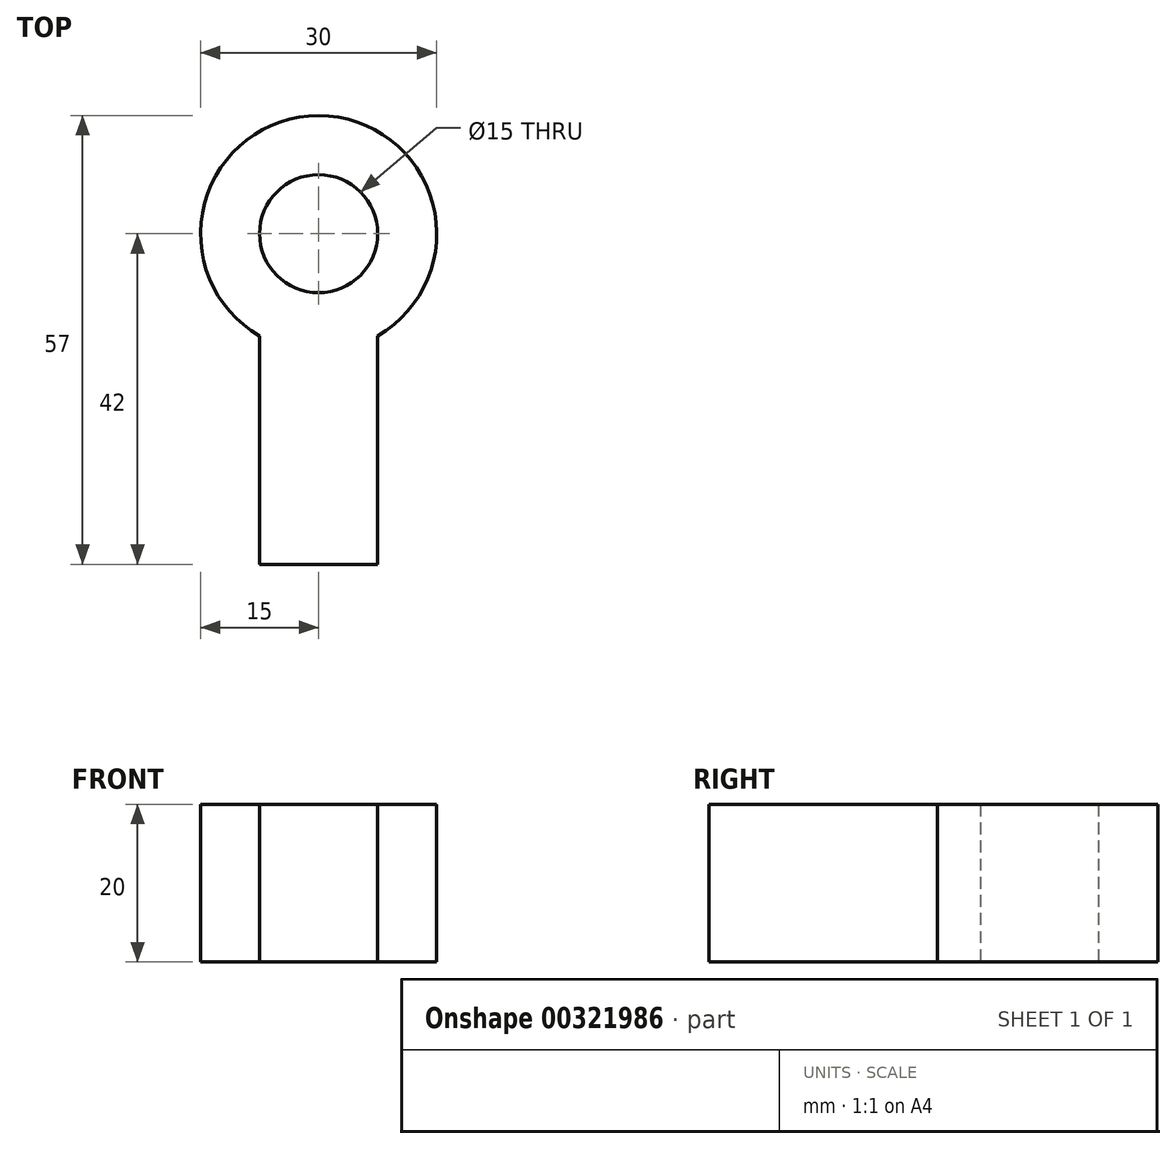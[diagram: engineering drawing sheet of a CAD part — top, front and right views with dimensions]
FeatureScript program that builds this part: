
annotation { "Feature Type Name" : "Feature", "Feature Type Description" : "" }
export const myFeature = defineFeature(function(context is Context, id is Id, definition is map)
    precondition{}
    {
        {
            var Q0;
            Q0=qCreatedBy(makeId("Top.planeOp"),FACE);
            var sketch = newSketch(context, id + "F0", { "sketchPlane" : qUnion([Q0])});
            skCircle(sketch, "E0", {"center": v(0, 0) * mm, "radius": 15 * mm});
            skCircle(sketch, "E1.0", {"center": v(0, 0) * mm, "radius": 7.5 * mm});
            skSolve(sketch);
        }
        {
            var Q0;
            Q0=makeQuery(id+"F0.imprint","IMPRINT",FACE,{"disambiguationData":[TD([[makeQuery(id+"F0.imprint","IMPRINT",EDGE,{"derivedFrom":sQuery(id+"F0.wireOp",EDGE,"E0")}),1.0]])]});
            extrude(context, id + "F1", {"entities" : qUnion([Q0]), "depth" : 20 * mm});
        }
        {
            var Q0;
            Q0=qCreatedBy(makeId("Front.planeOp"),FACE);
            cPlane(context, id + "F2", {"entities" : qUnion([Q0]), "cplaneType" : CPlaneType.OFFSET, "offset" : 12 * mm, "width" : 150 * mm, "height" : 150 * mm});
        }
        {
            var Q0;
            Q0=qCreatedBy(id+"F2.planeOp",FACE);
            var sketch = newSketch(context, id + "F3", { "sketchPlane" : qUnion([Q0])});
            skPoint(sketch, "E2", {"position": v(7.5, 0) * mm});
            skLineSegment(sketch, "E3.bottom", {"start": v(7.5, 0) * mm, "end": v(-7.5, 0) * mm});
            skLineSegment(sketch, "E3.top", {"start": v(7.5, 20) * mm, "end": v(-7.5, 20) * mm});
            skLineSegment(sketch, "E3.left", {"start": v(7.5, 0) * mm, "end": v(7.5, 20) * mm});
            skLineSegment(sketch, "E3.right", {"start": v(-7.5, 0) * mm, "end": v(-7.5, 20) * mm});
            skPoint(sketch, "E4", {"position": v(0, 0) * mm});
            skSolve(sketch);
        }
        {
            var Q0;
            Q0 = qSketchRegion(id + "F3", true);
            extrude(context, id + "F4", {"entities" : qUnion([Q0]), "operationType" : NewBodyOperationType.ADD, "depth" : 30 * mm});
        }
    });
